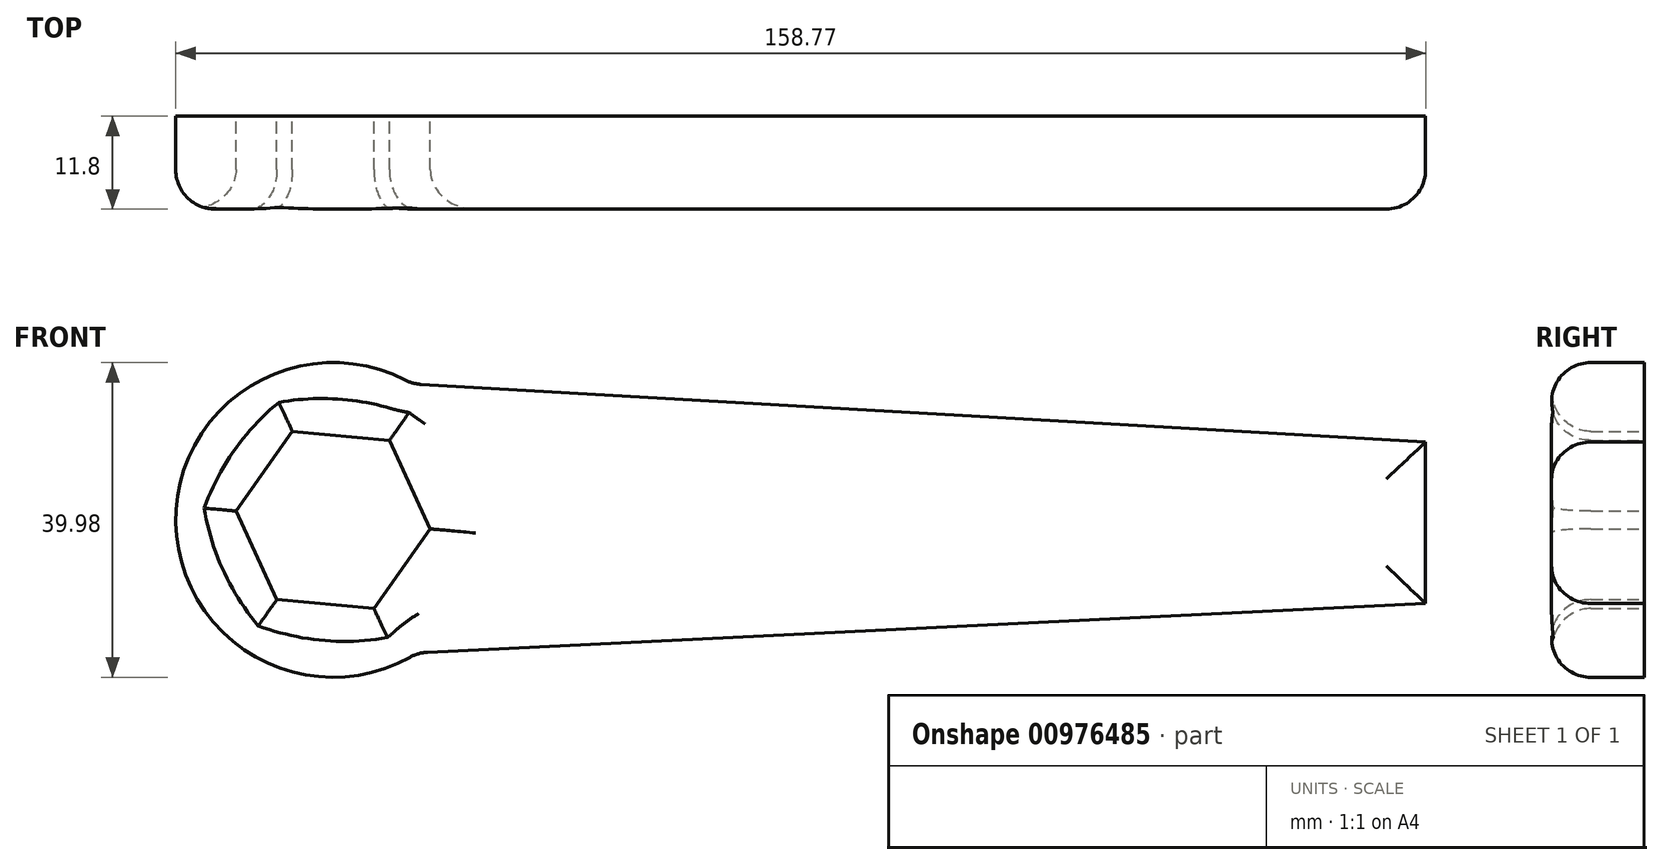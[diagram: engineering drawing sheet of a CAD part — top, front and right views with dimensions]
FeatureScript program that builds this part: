
annotation { "Feature Type Name" : "Feature", "Feature Type Description" : "" }
export const myFeature = defineFeature(function(context is Context, id is Id, definition is map)
    precondition{}
    {
        {
            var Q0;
            Q0=qCreatedBy(makeId("Front.planeOp"),FACE);
            var sketch = newSketch(context, id + "F0", { "sketchPlane" : qUnion([Q0])});
            skCircle(sketch, "E0.cCircle", {"center": v(-56.64, 0) * mm, "radius": 10.73 * mm, "construction": true});
            skLineSegment(sketch, "E0.0", {"start": v(-44.3, -1.13) * mm, "end": v(-51.45, -11.25) * mm});
            skLineSegment(sketch, "E0.1", {"start": v(-51.45, -11.25) * mm, "end": v(-63.79, -10.12) * mm});
            skLineSegment(sketch, "E0.2", {"start": v(-63.79, -10.12) * mm, "end": v(-68.97, 1.13) * mm});
            skLineSegment(sketch, "E0.3", {"start": v(-68.97, 1.13) * mm, "end": v(-61.82, 11.25) * mm});
            skLineSegment(sketch, "E0.4", {"start": v(-61.82, 11.25) * mm, "end": v(-49.48, 10.12) * mm});
            skLineSegment(sketch, "E0.5", {"start": v(-49.48, 10.12) * mm, "end": v(-44.3, -1.13) * mm});
            skPoint(sketch, "E0.0.midPoint", {"position": v(-47.87, -6.2) * mm});
            skArc(sketch, "E1", {"start": v(-47.47, 17.77) * mm, "mid": v(-76.63, -0.35) * mm, "end": v(-46.85, -17.43) * mm});
            skLineSegment(sketch, "E2", {"start": v(-45.47, 17.22) * mm, "end": v(82.14, 9.9) * mm});
            skLineSegment(sketch, "E3", {"start": v(82.14, 9.9) * mm, "end": v(82.14, -10.62) * mm});
            skLineSegment(sketch, "E4", {"start": v(82.14, -10.62) * mm, "end": v(-44.65, -16.8) * mm});
            skPoint(sketch, "E5.visualSharp", {"position": v(-46.6, 17.29) * mm});
            skArc(sketch, "E5.filletArc", {"start": v(-47.47, 17.77) * mm, "mid": v(-46.5, 17.4) * mm, "end": v(-45.47, 17.22) * mm});
            skPoint(sketch, "E6.visualSharp", {"position": v(-45.9, -16.86) * mm});
            skArc(sketch, "E6.filletArc", {"start": v(-44.65, -16.8) * mm, "mid": v(-45.79, -17) * mm, "end": v(-46.85, -17.43) * mm});
            skSolve(sketch);
        }
        {
            var Q0;
            Q0=makeQuery(id+"F0.imprint","IMPRINT",FACE,{"disambiguationData":[TD([[makeQuery(id+"F0.imprint","IMPRINT",EDGE,{"derivedFrom":sQuery(id+"F0.wireOp",EDGE,"E0.0")}),1.0]])]});
            extrude(context, id + "F1", {"entities" : qUnion([Q0]), "depth" : 11.8 * mm, "offsetDistance" : 25 * mm});
        }
        {
            var Q0;
            Q0=makeQuery(id+"F1.opExtrude","CAP_FACE",FACE,{"disambiguationData":[OSD([sQuery(id+"F0.wireOp",EDGE,"E0.0"),sQuery(id+"F0.wireOp",EDGE,"E0.1"),sQuery(id+"F0.wireOp",EDGE,"E0.2"),sQuery(id+"F0.wireOp",EDGE,"E0.3"),sQuery(id+"F0.wireOp",EDGE,"E0.4"),sQuery(id+"F0.wireOp",EDGE,"E0.5"),sQuery(id+"F0.wireOp",EDGE,"E1"),sQuery(id+"F0.wireOp",EDGE,"E2"),sQuery(id+"F0.wireOp",EDGE,"E3"),sQuery(id+"F0.wireOp",EDGE,"E4"),sQuery(id+"F0.wireOp",EDGE,"E5.filletArc"),sQuery(id+"F0.wireOp",EDGE,"E6.filletArc")])],"isStart":false});
            fillet(context, id + "F2", {"entities" : qUnion([Q0]), "radius" : 5 * mm, "tangentPropagation" : true, "allowEdgeOverflow" : false});
        }
    });
